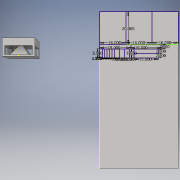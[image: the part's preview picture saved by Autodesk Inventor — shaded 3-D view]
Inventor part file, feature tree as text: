
AUTODESK INVENTOR PART (.ipt)
format: ipt  version: 2016 (Build 200138000, 138)  size: 245,760 bytes
history: native  units: in
note: dims shown in document units (in); Inventor stores cm internally (conversion verified against a paired STEP export)
features: sketch x10, extrude x8, plane x1, loft x1
ambient origin geometry x8: Origin, YZ Plane, XZ Plane, XY Plane, X Axis, Y Axis, Z Axis, Center Point
bodies: Solid1 (feature_tree)
feature tree (20):
  extrude  "Extrusion1"  Depth=20.0in
  sketch  "Sketch2"  dims[d2=16.0in d3=0.0in d4=11.75in]
  plane  "Work Plane1"
  loft  "Loft1"
  extrude  "Extrusion2"  Depth=6.5in
  extrude  "Extrusion3"  TaperAngle=0.0deg  [1 undecoded]
  extrude  "Extrusion4"  Depth=13.3in
  extrude  "Extrusion5"  Depth=2.56in
  extrude  "Extrusion6"  Depth=15.3775in TaperAngle=0.0deg
  extrude  "Extrusion7"  Depth=5.5in TaperAngle=0.0deg
  extrude  "Extrusion8"  Depth=1.0in TaperAngle=0.0deg
  sketch  "Sketch11"  dims[d30=1.0in d31=1.0in d32=1.0in d33=1.0in d34=2.8in d35=0.0in d36=1.0in d37=16.0in d38=0.0in d39=48.0in d40=96.0in d41=0.75in d42=0.0in d43=20.0in d44=16.0in d45=16.0in d46=16.0in d47=2.8in d48=19.0in d49=19.0in d53=5.5in d54=1.5in d55=1.5in d56=1.5in d57=1.5in d58=1.5in d59=1.5in d60=3.0in d61=3.0in d62=3.0in d63=3.0in d64=5.5in d65=15.0in d66=2.8in d67=2.8in]
  sketch  "Sketch1"  dims[d0=1.0in d1=20.0in]
  sketch  "Sketch3"  dims[d5=6.5in d6=2.5in]
  sketch  "Sketch4"  dims[d7=0.0in d8=90.0deg d9=0.0in d10=90.0deg]
  sketch  "Sketch6"  dims[d11=16.2in d12=13.3in]
  sketch  "Sketch7"  dims[d13=2.56in d14=0.0in d15=0.94in]
  sketch  "Sketch8"  dims[d16=8.1in d17=15.3775in d18=0.0in]
  sketch  "Sketch9"  dims[d19=3.0in d20=5.5in d21=0.0in]
  sketch  "Sketch10"  dims[d22=1.25in d23=1.25in d24=1.25in d25=1.25in d26=1.25in d27=1.25in d28=1.0in d29=0.0in]
note: 1 required parameter value undecoded (feature->parameter linkage not recoverable at this tier; creation-order binding heuristic only, values carry confidence <= 0.55)
